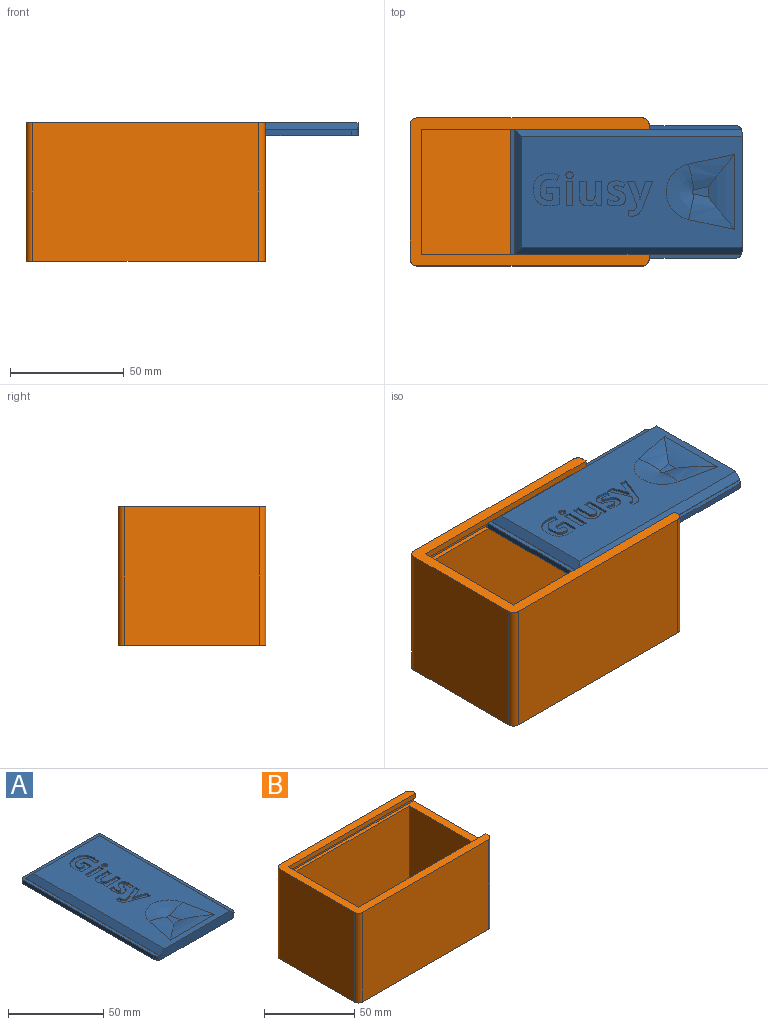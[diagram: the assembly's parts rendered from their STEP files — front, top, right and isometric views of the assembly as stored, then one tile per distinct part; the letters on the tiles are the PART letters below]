
ASSEMBLY  parts=2 mates=1
PART A: 116 faces, bbox 69.6x101.6x5.8 mm
  f0: plane 96.82x48.72mm, normal (0,0,1), area 3626.3mm2, adj f4,f10,f11,f12,f14,f15,f16,f17
  f1: plane 97.3x2.6mm, normal (1,0,0), area 253mm2, adj f5,f6,f112,f114
  f2: plane 55.7x2.6mm, normal (0,1,0), area 144.8mm2, adj f5,f6,f112,f113
  f3: plane 97.3x2.6mm, normal (-1,0,0), area 253mm2, adj f5,f6,f113,f115
  f4: plane 52.3x5.8mm, normal (0,-1,0), area 300.1mm2, adj f0,f6,f10,f11,f114,f115
  f5: plane 101.35x58.3mm, normal (0,0,1), area 459.8mm2, adj f1,f2,f3,f7,f8,f9,f112,f113
  f6: plane 101.6x58.3mm, normal (0,0,-1), area 5918.7mm2, adj f1,f2,f3,f4,f112,f113,f114,f115
  f7: plane 54.7x0.2mm, normal (0,1,0), area 10.9mm2, adj f5,f8,f9,f12
  f8: plane 99.55x0.2mm, normal (1,0,0), area 19.9mm2, adj f5,f7,f10,f114
  f9: plane 99.55x0.2mm, normal (-1,0,0), area 19.9mm2, adj f5,f7,f11,f115
  f10: plane 99.83x3.03mm, normal (0.71,0,0.71), area 416.9mm2, adj f0,f4,f8,f12,f114
  f11: plane 99.83x3.03mm, normal (-0.71,0,0.71), area 416.9mm2, adj f0,f4,f9,f12,f115
  f12: plane 54.7x3mm, normal (0,0.71,0.71), area 219.3mm2, adj f0,f7,f10,f11
  f13: plane 7.01x4.6mm, normal (0,0,1), area 21.5mm2, adj f14,f15,f16,f17
  f14: bspline ~22.47x15.51mm, area 157.5mm2, adj f0,f13,f15,f16
  f15: bspline ~24.43x12.28mm, area 213.3mm2, adj f0,f13,f14,f17
  f16: bspline ~57.85x11.49mm, area 220.1mm2, adj f0,f13,f14,f17
  f17: bspline ~22.47x15.51mm, area 157.5mm2, adj f0,f13,f15,f16
  f18: plane 10.54x4.22mm, normal (0.37,-0.93,0), area 11.4mm2, adj f0,f19,f34,f35
  f19: plane 1x0.52mm, normal (-0.31,-0.95,0), area 0.6mm2, adj f0,f18,f20,f35
  f20: extruded ~1.42x1mm, area 1.7mm2, adj f0,f19,f21,f35
  f21: extruded ~1.34x1mm, area 1.5mm2, adj f0,f20,f22,f35
  f22: extruded ~1.14x1mm, area 1.1mm2, adj f0,f21,f23,f35
  f23: plane 2.3x1mm, normal (0,-1,0), area 2.3mm2, adj f0,f22,f24,f35
  f24: extruded ~1.47x1mm, area 1.5mm2, adj f0,f23,f25,f35
  f25: extruded ~2.67x1mm, area 2.8mm2, adj f0,f24,f26,f35
  f26: extruded ~2.49x1.76mm, area 3.1mm2, adj f0,f25,f27,f35
  f27: plane 11.97x4.49mm, normal (0.35,0.94,0), area 12.8mm2, adj f0,f26,f28,f35
  f28: plane 3.11x1mm, normal (-1,0,0), area 3.1mm2, adj f0,f27,f29,f35
  f29: plane 5.97x1.97mm, normal (-0.31,-0.95,0), area 6.3mm2, adj f0,f28,f30,f35
  f30: extruded ~1.84x1mm, area 1.9mm2, adj f0,f29,f31,f35
  f31: plane 1x0.06mm, normal (-1,0,0), area 0.1mm2, adj f0,f30,f32,f35
  f32: extruded ~1.84x1mm, area 1.9mm2, adj f0,f31,f33,f35
  f33: plane 5.97x2mm, normal (-0.32,0.95,0), area 6.3mm2, adj f0,f32,f34,f35
  f34: plane 3.17x1mm, normal (-1,0,0), area 3.2mm2, adj f0,f18,f33,f35
  f35: plane 15.29x11.06mm, normal (0,0,1), area 73.6mm2, adj f18,f19,f20,f21,f22,f23,f24,f25
  f36: extruded ~1.36x1mm, area 1.4mm2, adj f0,f37,f61,f62
  f37: extruded ~1.01x1mm, area 1.3mm2, adj f0,f36,f38,f62
  f38: extruded ~1.82x1mm, area 2.1mm2, adj f0,f37,f39,f62
  f39: extruded ~1.81x1mm, area 2mm2, adj f0,f38,f40,f62
  f40: extruded ~1x0.67mm, area 0.8mm2, adj f0,f39,f41,f62
  f41: extruded ~1.28x1mm, area 1.6mm2, adj f0,f40,f42,f62
  f42: extruded ~1.42x1mm, area 1.4mm2, adj f0,f41,f43,f62
  f43: extruded ~1.49x1mm, area 1.6mm2, adj f0,f42,f44,f62
  f44: plane 2.09x1mm, normal (0.39,0.92,0), area 2.3mm2, adj f0,f43,f45,f62
  f45: extruded ~3.73x1mm, area 3.9mm2, adj f0,f44,f46,f62
  f46: extruded ~3.11x1mm, area 3.3mm2, adj f0,f45,f47,f62
  f47: extruded ~2.19x1.1mm, area 2.6mm2, adj f0,f46,f48,f62
  f48: extruded ~1.39x1mm, area 1.4mm2, adj f0,f47,f49,f62
  f49: extruded ~1x1mm, area 1.3mm2, adj f0,f48,f50,f62
  f50: extruded ~1.8x1mm, area 2mm2, adj f0,f49,f51,f62
  f51: extruded ~1.37x1mm, area 1.5mm2, adj f0,f50,f52,f62
  f52: extruded ~1x0.72mm, area 0.9mm2, adj f0,f51,f53,f62
  f53: extruded ~1x0.56mm, area 0.6mm2, adj f0,f52,f54,f62
  f54: extruded ~1.58x1mm, area 2mm2, adj f0,f53,f55,f62
  f55: extruded ~1.78x1mm, area 1.8mm2, adj f0,f54,f56,f62
  f56: extruded ~1.82x1mm, area 1.9mm2, adj f0,f55,f57,f62
  f57: plane 2.39x1mm, normal (0,-1,0), area 2.4mm2, adj f0,f56,f58,f62
  f58: extruded ~1.53x1mm, area 1.6mm2, adj f0,f57,f59,f62
  f59: extruded ~1.98x1mm, area 2mm2, adj f0,f58,f60,f62
  f60: extruded ~3.4x1mm, area 3.6mm2, adj f0,f59,f61,f62
  f61: extruded ~2.49x1.13mm, area 2.8mm2, adj f0,f36,f60,f62
  f62: plane 11x8.05mm, normal (0,0,1), area 56.4mm2, adj f36,f37,f38,f39,f40,f41,f42,f43
  f63: plane 2.22x1mm, normal (1,0,0), area 2.2mm2, adj f0,f64,f79,f80
  f64: plane 10.62x1mm, normal (0,1,0), area 10.6mm2, adj f0,f63,f65,f80
  f65: plane 2.9x1mm, normal (-1,0,0), area 2.9mm2, adj f0,f64,f66,f80
  f66: plane 4.99x1mm, normal (0,-1,0), area 5mm2, adj f0,f65,f67,f80
  f67: extruded ~2.69x1mm, area 2.8mm2, adj f0,f66,f68,f80
  f68: extruded ~1.76x1mm, area 2mm2, adj f0,f67,f69,f80
  f69: extruded ~1.3x1mm, area 1.5mm2, adj f0,f68,f70,f80
  f70: extruded ~1.72x1mm, area 1.8mm2, adj f0,f69,f71,f80
  f71: plane 6.2x1mm, normal (0,1,0), area 6.2mm2, adj f0,f70,f72,f80
  f72: plane 2.9x1mm, normal (-1,0,0), area 2.9mm2, adj f0,f71,f73,f80
  f73: plane 6.92x1mm, normal (0,-1,0), area 6.9mm2, adj f0,f72,f74,f80
  f74: extruded ~2.88x1mm, area 3.1mm2, adj f0,f73,f75,f80
  f75: extruded ~2.82x1mm, area 3.1mm2, adj f0,f74,f76,f80
  f76: extruded ~1.95x1mm, area 2mm2, adj f0,f75,f77,f80
  f77: extruded ~1.32x1.15mm, area 1.8mm2, adj f0,f76,f78,f80
  f78: plane 1x0.15mm, normal (1,0,0), area 0.2mm2, adj f0,f77,f79,f80
  f79: plane 1.36x1mm, normal (0.28,-0.96,0), area 1.4mm2, adj f0,f63,f78,f80
  f80: plane 10.81x9.8mm, normal (0,0,1), area 68.8mm2, adj f63,f64,f65,f66,f67,f68,f69,f70
  f81: plane 10.62x1mm, normal (0,1,0), area 10.6mm2, adj f0,f82,f84,f85
  f82: plane 2.9x1mm, normal (-1,0,0), area 2.9mm2, adj f0,f81,f83,f85
  f83: plane 10.62x1mm, normal (0,-1,0), area 10.6mm2, adj f0,f82,f84,f85
  f84: plane 2.9x1mm, normal (1,0,0), area 2.9mm2, adj f0,f81,f83,f85
  f85: plane 10.62x2.9mm, normal (0,0,1), area 30.7mm2, adj f81,f82,f83,f84
  f86: extruded ~1.58x1.43mm, area 2.4mm2, adj f0,f87,f90,f91
  f87: extruded ~1.18x1mm, area 1.3mm2, adj f0,f86,f88,f91
  f88: extruded ~1.05x1mm, area 1.2mm2, adj f0,f87,f89,f91
  f89: extruded ~1.58x1.42mm, area 2.4mm2, adj f0,f88,f90,f91
  f90: extruded ~1.58x1.42mm, area 2.4mm2, adj f0,f86,f89,f91
  f91: plane 3.15x2.84mm, normal (0,0,1), area 7.5mm2, adj f86,f87,f88,f89,f90
  f92: plane 2.45x1mm, normal (0,-1,0), area 2.5mm2, adj f0,f93,f110,f111
  f93: plane 2.63x1mm, normal (1,0,0), area 2.6mm2, adj f0,f92,f94,f111
  f94: plane 2.9x1mm, normal (0,-1,0), area 2.9mm2, adj f0,f93,f95,f111
  f95: extruded ~1.87x1mm, area 1.9mm2, adj f0,f94,f96,f111
  f96: extruded ~2.69x1.19mm, area 3.1mm2, adj f0,f95,f97,f111
  f97: extruded ~3.45x1mm, area 3.6mm2, adj f0,f96,f98,f111
  f98: extruded ~3.45x1.15mm, area 3.7mm2, adj f0,f97,f99,f111
  f99: extruded ~3.06x1.28mm, area 3.4mm2, adj f0,f98,f100,f111
  f100: extruded ~3.16x1mm, area 3.3mm2, adj f0,f99,f101,f111
  f101: plane 2.35x1mm, normal (0.38,0.92,0), area 2.5mm2, adj f0,f100,f102,f111
  f102: extruded ~4.12x1mm, area 4.2mm2, adj f0,f101,f103,f111
  f103: extruded ~5.33x1.88mm, area 5.8mm2, adj f0,f102,f104,f111
  f104: extruded ~5.24x1.92mm, area 5.7mm2, adj f0,f103,f105,f111
  f105: extruded ~5.3x1.66mm, area 5.7mm2, adj f0,f104,f106,f111
  f106: extruded ~4.8x1.85mm, area 5.3mm2, adj f0,f105,f107,f111
  f107: extruded ~2.42x1mm, area 2.4mm2, adj f0,f106,f108,f111
  f108: extruded ~2.52x1mm, area 2.6mm2, adj f0,f107,f109,f111
  f109: plane 7.2x1mm, normal (0,1,0), area 7.2mm2, adj f0,f108,f110,f111
  f110: plane 5.51x1mm, normal (-1,0,0), area 5.5mm2, adj f0,f92,f109,f111
  f111: plane 14.27x11.39mm, normal (0,0,1), area 93.9mm2, adj f92,f93,f94,f95,f96,f97,f98,f99
  f112: cylinder r=1.3mm len=2.6mm, axis (0,0,1), area 5.3mm2, adj f1,f2,f5,f6
  f113: cylinder r=1.3mm len=2.6mm, axis (0,0,-1), area 5.3mm2, adj f2,f3,f5,f6
  f114: cylinder r=3mm len=4mm, axis (0,0,-1), area 13.2mm2, adj f1,f4,f5,f6,f8,f10
  f115: cylinder r=3mm len=4mm, axis (0,0,1), area 13.2mm2, adj f3,f4,f5,f6,f9,f11
PART B: 27 faces, bbox 105x65x61 mm
  f0: plane 59x55mm, normal (1,0,0), area 3245mm2, adj f13,f15,f20,f23
  f1: plane 3x2mm, normal (1,0,0), area 6mm2, adj f2,f16,f23,f26
  f2: plane 100x3mm, normal (0,1,0), area 300mm2, adj f1,f3,f16,f26
  f3: plane 55x3mm, normal (1,0,0), area 165mm2, adj f2,f9,f16,f26
  f4: plane 95x50mm, normal (0,-1,0), area 4750mm2, adj f5,f11,f14,f15
  f5: plane 55x50mm, normal (-1,0,0), area 2750mm2, adj f4,f10,f14,f15
  f6: plane 3x2mm, normal (1,0,0), area 6mm2, adj f9,f16,f20,f26
  f7: plane 99x61mm, normal (0,1,0), area 6039mm2, adj f13,f20,f21,f26
  f8: plane 61x59mm, normal (-1,0,0), area 3599mm2, adj f13,f21,f22,f26
  f9: plane 100x3mm, normal (0,-1,0), area 300mm2, adj f3,f6,f16,f26
  f10: plane 95x50mm, normal (0,1,0), area 4750mm2, adj f5,f11,f14,f15
  f11: plane 55x50mm, normal (1,0,0), area 2750mm2, adj f4,f10,f14,f15
  f12: plane 99x61mm, normal (0,-1,0), area 6039mm2, adj f13,f22,f23,f26
  f13: plane 105x65mm, normal (0,0,-1), area 6817.3mm2, adj f0,f7,f8,f12,f20,f21,f22,f23
  f14: plane 95x55mm, normal (0,0,1), area 5225mm2, adj f4,f5,f10,f11
  f15: plane 102x59mm, normal (0,0,1), area 792mm2, adj f0,f4,f5,f10,f11,f17,f18,f19
  f16: plane 102x59mm, normal (0,0,-1), area 517mm2, adj f1,f2,f3,f6,f9,f17,f18,f19
  f17: plane 100.5x3mm, normal (0,-1,0), area 301.5mm2, adj f15,f16,f20,f25
  f18: plane 56x3mm, normal (1,0,0), area 168mm2, adj f15,f16,f24,f25
  f19: plane 100.5x3mm, normal (0,1,0), area 301.5mm2, adj f15,f16,f23,f24
  f20: cylinder r=3mm len=61mm, axis (0,0,-1), area 287.5mm2, adj f0,f6,f7,f13,f17,f26
  f21: cylinder r=3mm len=61mm, axis (0,0,1), area 287.5mm2, adj f7,f8,f13,f26
  f22: cylinder r=3mm len=61mm, axis (0,0,-1), area 287.5mm2, adj f8,f12,f13,f26
  f23: cylinder r=3mm len=61mm, axis (0,0,1), area 287.5mm2, adj f0,f1,f12,f13,f19,f26
  f24: cylinder r=1.5mm len=3mm, axis (0,0,1), area 7.1mm2, adj f15,f16,f18,f19
  f25: cylinder r=1.5mm len=3mm, axis (0,0,1), area 7.1mm2, adj f15,f16,f17,f18
  f26: plane 105x65mm, normal (0,0,1), area 1317.3mm2, adj f1,f2,f3,f6,f7,f8,f9,f12
PLACE A rot(axis=(0,0,1),90deg) t=(20.52,-0.65,66.72)mm
PLACE B t=(-22,-0.65,11.52)mm fixed
MATE slider A.f2 <-> B.f18  axis (-1,0,0) through (-30.28,-0.65,68.02)mm
